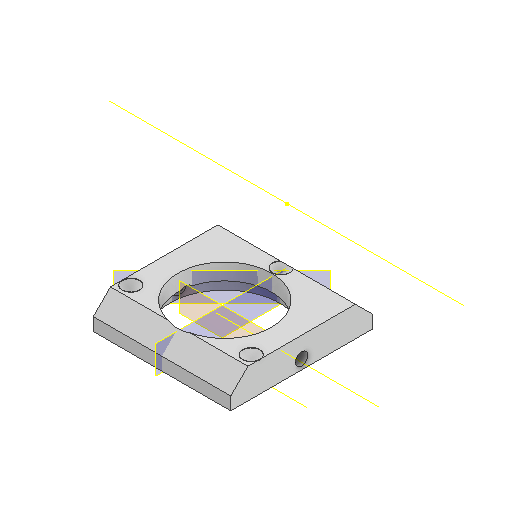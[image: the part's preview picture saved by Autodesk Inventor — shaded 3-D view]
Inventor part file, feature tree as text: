
AUTODESK INVENTOR PART (.ipt)
format: ipt  version: 2022 (Build 260153000, 153)  size: 225,792 bytes
history: native  units: mm
features: sketch x10, extrude x8, other x8, projected_geometry x7, plane x6, reference x4, hole x1, chamfer x1
ambient origin geometry x8: Origin, YZ Plane, XZ Plane, XY Plane, X Axis, Y Axis, Z Axis, Center Point
bodies: Volumenkörper1 (feature_tree)
feature tree (45):
  extrude  "Extrusion1"  Depth=28.0mm
  plane  "Arbeitsebene2"
  plane  "Arbeitsebene3"
  extrude  "Extrusion6"  Depth=5.0mm
  plane  "Arbeitsebene4"
  sketch  "Skizze7"  dims[d25=6.0mm d26=0.0mm d27=3.0mm]
  extrude  "Extrusion7"  Depth=3.0mm
  plane  "Arbeitsebene5"
  extrude  "Extrusion9"  Depth=7.0mm TaperAngle=0.0deg
  plane  "Arbeitsebene6"
  extrude  "Extrusion10"  TaperAngle=0.0deg  [1 undecoded]
  extrude  "Extrusion11"  Depth=4.0mm TaperAngle=0.0deg
  hole  "Bohrung2"  [1 undecoded]
  chamfer  "Fase3"  Distance=3.2mm
  extrude  "Extrusion12"  Depth=0.1mm
  extrude  "Extrusion13"  [1 undecoded]
  sketch  "Skizze1"  dims[d0=18.0mm d1=28.0mm]
  plane  "Arbeitsebene1"
  sketch  "Skizze6"  dims[d2=7.0mm d3=0.0mm d24=5.0mm]
  projected_geometry  "Projizierte Kontur6"
  sketch  "Skizze8"  dims[d28=3.0mm d29=7.0mm d30=0.0mm]
  projected_geometry  "Projizierte Kontur7"
  sketch  "Skizze10"  dims[d38=2.9mm d39=0.0mm d40=0.0mm]
  projected_geometry  "Projizierte Kontur8"
  sketch  "Skizze13"  dims[d48=4.0mm d49=6.0mm d50=4.0mm d51=2.0mm d52=90.0deg d53=0.1mm d54=20.594885mm d63=4.0mm d64=0.0mm]
  sketch  "Skizze15"  dims[d65=4.0mm d66=0.0mm d67=4.0mm d68=2.0mm d69=45.0deg]
  projected_geometry  "Projizierte Kontur12"
  sketch  "Skizze16"  dims[d70=25.0mm d71=3.2mm d72=0.0mm]
  projected_geometry  "Projizierte Kontur13"
  reference  "Referenz1"
  reference  "Referenz2"
  reference  "Referenz4"
  sketch  "Sketch17"  dims[d73=0.0mm d74=0.0mm d75=0.1mm]
  projected_geometry  "Projected Loop14"
  sketch  "Sketch18"
  projected_geometry  "Projected Loop15"
  reference  "Reference5"
  other  "Assembly_Cube_Fibercombiner_v3.iam"
  other  "DIN 912 - ersetzt durch DIN EN ISO 4762 M3 x 25:3"
  other  "DIN 912 - ersetzt durch DIN EN ISO 4762 M3 x 25:1"
  other  "DIN 912 - ersetzt durch DIN EN ISO 4762 M3 x 25:2"
  other  "<userpath> Lab\Documents\UC2-INVENTOR-Git\uc2_v3\Assembly_Cube_Fibercombiner_v3.iam"
  other  "00_DMLP425-Step:1"
  other  "Assembly_Cube_empty_IM_v3:2"
  other  "10_Cube_1x1_IM:1"
note: 3 required parameter values undecoded (feature->parameter linkage not recoverable at this tier; creation-order binding heuristic only, values carry confidence <= 0.55)
